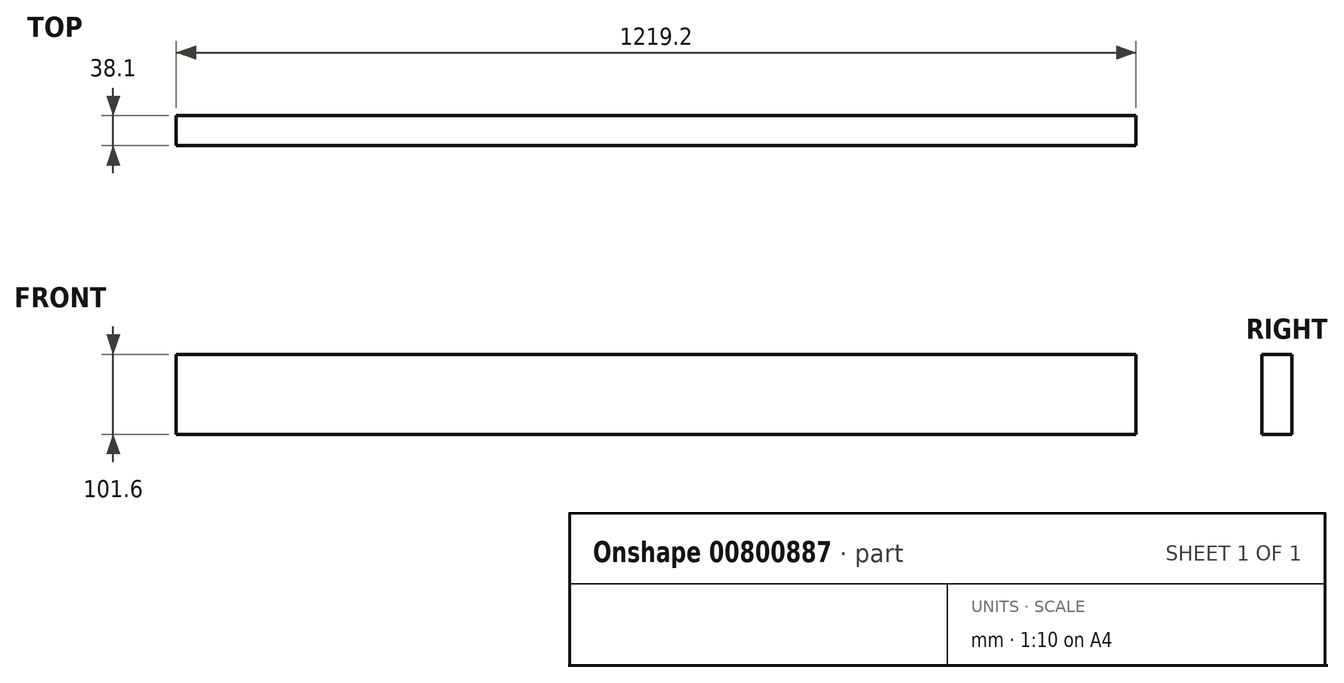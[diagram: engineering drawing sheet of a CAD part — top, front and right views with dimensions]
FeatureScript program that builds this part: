
annotation { "Feature Type Name" : "Feature", "Feature Type Description" : "" }
export const myFeature = defineFeature(function(context is Context, id is Id, definition is map)
    precondition{}
    {
        {
            var Q0;
            Q0=qCreatedBy(makeId("Front.planeOp"),FACE);
            var sketch = newSketch(context, id + "F0", { "sketchPlane" : qUnion([Q0])});
            skLineSegment(sketch, "E0.bottom", {"start": v(-608.58, 107.27) * mm, "end": v(610.62, 107.27) * mm});
            skLineSegment(sketch, "E0.top", {"start": v(-608.58, 5.67) * mm, "end": v(610.62, 5.67) * mm});
            skLineSegment(sketch, "E0.left", {"start": v(-608.58, 107.27) * mm, "end": v(-608.58, 5.67) * mm});
            skLineSegment(sketch, "E0.right", {"start": v(610.62, 107.27) * mm, "end": v(610.62, 5.67) * mm});
            skSolve(sketch);
        }
        {
            var Q0;
            Q0=makeQuery(id+"F0.imprint","IMPRINT",FACE,{"disambiguationData":[TD([[makeQuery(id+"F0.imprint","IMPRINT",EDGE,{"derivedFrom":sQuery(id+"F0.wireOp",EDGE,"E0.bottom")}),-1.0]])]});
            extrude(context, id + "F1", {"entities" : qUnion([Q0]), "depth" : 38.1 * mm, "offsetDistance" : 25.4 * mm});
        }
    });
